# Revit family: 201_FINO-_
name_source: partatom
category: Air Terminals
units: mm (PartAtom-declared; Revit-internal decimal feet)

## family parameters
Always vertical = Yes
Cut with Voids When Loaded = No
Part Type = Normal
Room Calculation Point = Yes
Round Connector Dimension = Use Diameter
Shared = No
Work Plane-Based = No

## types (1)
- FINO-160
    A2 = 125 mm  [stored 0.410105 ft]
    B2 = 100 mm  [stored 0.328084 ft]
    C = 12 mm  [stored 0.0393701 ft]
    CAT0 = Yes
    CLBTZ = 0 mm  [stored 0 ft]
    CL_Location_5000 = 5000 mm  [stored 16.4042 ft]
    C__ve = -12 mm  [stored -0.0393701 ft]
    D = 160 mm
    Description = Supply air diffuser for wall mounting
    H_ARR = 0 mm  [stored 0 ft]
    L_ARR = 400 mm  [stored 1.31234 ft]
    MC Product Code = FINO-160
    Manufacturer = Climecon
    QmdConnectorList = 201;D
    URL = www.climecon.fi
    W_ARR = 400 mm  [stored 1.31234 ft]
    magiPartTypeId = 201
    magiProductFamilyId = FINO-*
    magiProductId = FINO-160

note: [stored X ft] marks values corroborated as IEEE doubles in the binary element streams (Revit-internal decimal feet)

## geometry (parser evidence)
native form markers: Sweep x1
no freeform markers — native parametric forms only
